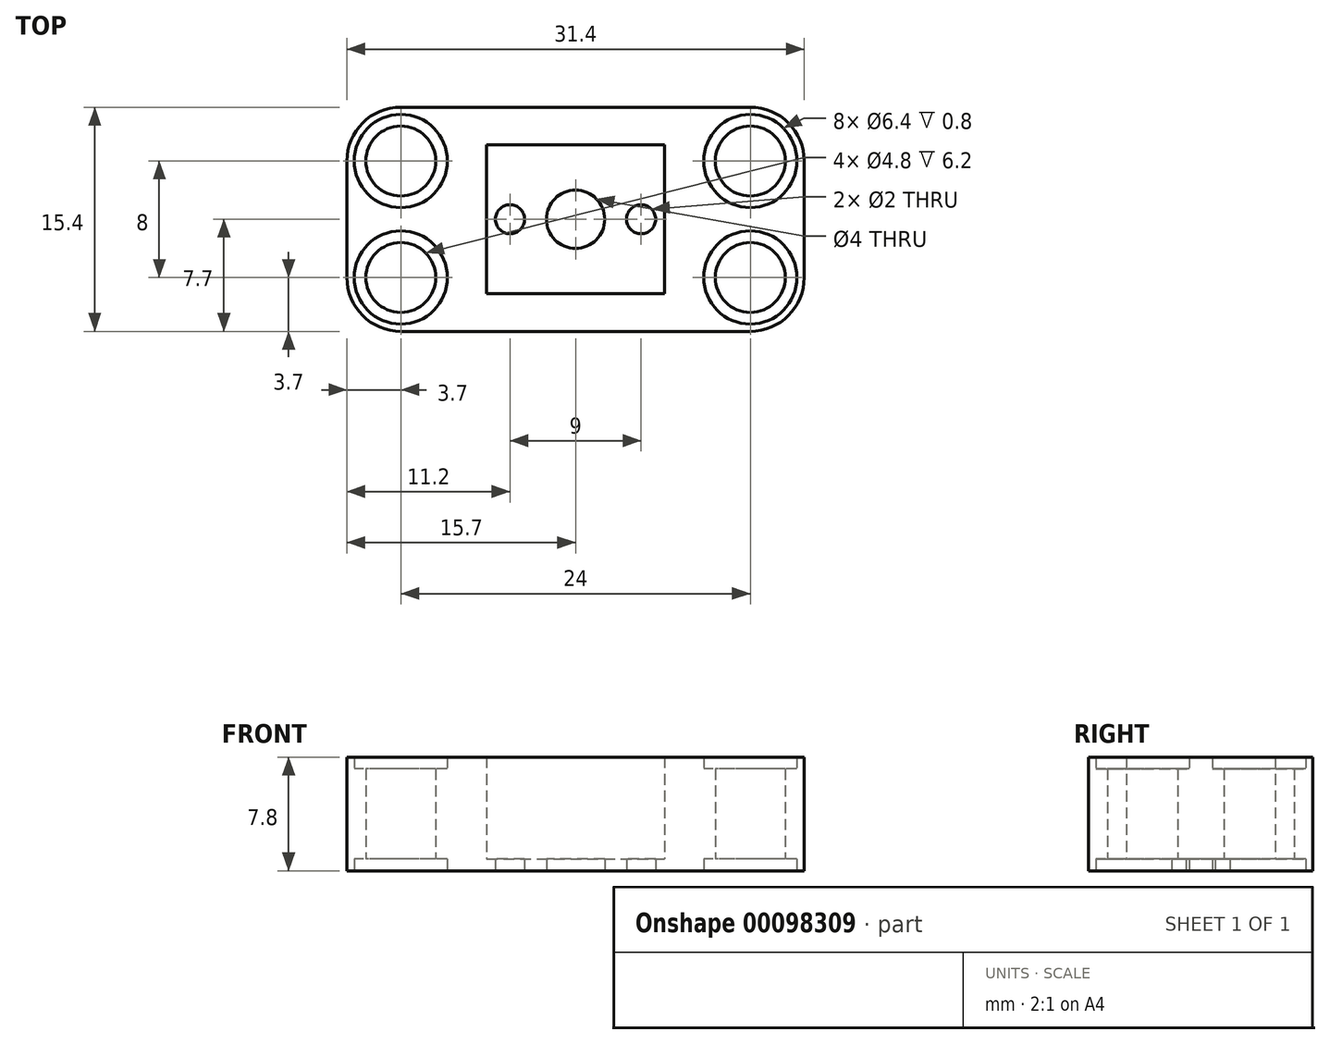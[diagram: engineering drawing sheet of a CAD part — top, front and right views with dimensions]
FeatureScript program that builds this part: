
annotation { "Feature Type Name" : "Feature", "Feature Type Description" : "" }
export const myFeature = defineFeature(function(context is Context, id is Id, definition is map)
    precondition{}
    {
        {
            var Q0;
            Q0=qCreatedBy(makeId("Top.planeOp"),FACE);
            var sketch = newSketch(context, id + "F0", { "sketchPlane" : qUnion([Q0])});
            skLineSegment(sketch, "E0.bottom", {"start": v(-12, 7.7) * mm, "end": v(12, 7.7) * mm});
            skLineSegment(sketch, "E0.top", {"start": v(-12, -7.7) * mm, "end": v(12, -7.7) * mm});
            skLineSegment(sketch, "E0.left", {"start": v(-15.7, 4) * mm, "end": v(-15.7, -4) * mm});
            skLineSegment(sketch, "E0.right", {"start": v(15.7, 4) * mm, "end": v(15.7, -4) * mm});
            skPoint(sketch, "E1.visualSharp", {"position": v(15.7, 7.7) * mm});
            skArc(sketch, "E1.filletArc", {"start": v(15.7, 4) * mm, "mid": v(14.62, 6.62) * mm, "end": v(12, 7.7) * mm});
            skPoint(sketch, "E2.visualSharp", {"position": v(15.7, -7.7) * mm});
            skArc(sketch, "E2.filletArc", {"start": v(12, -7.7) * mm, "mid": v(14.62, -6.62) * mm, "end": v(15.7, -4) * mm});
            skPoint(sketch, "E3.visualSharp", {"position": v(-15.7, -7.7) * mm});
            skArc(sketch, "E3.filletArc", {"start": v(-15.7, -4) * mm, "mid": v(-14.62, -6.62) * mm, "end": v(-12, -7.7) * mm});
            skPoint(sketch, "E4.visualSharp", {"position": v(-15.7, 7.7) * mm});
            skArc(sketch, "E4.filletArc", {"start": v(-12, 7.7) * mm, "mid": v(-14.62, 6.62) * mm, "end": v(-15.7, 4) * mm});
            skCircle(sketch, "E5", {"center": v(-12, 4) * mm, "radius": 3.2 * mm});
            skCircle(sketch, "E6", {"center": v(-12, 4) * mm, "radius": 2.4 * mm});
            skCircle(sketch, "E7", {"center": v(12, 4) * mm, "radius": 2.4 * mm});
            skCircle(sketch, "E8", {"center": v(12, 4) * mm, "radius": 3.2 * mm});
            skCircle(sketch, "E9", {"center": v(-12, -4) * mm, "radius": 2.4 * mm});
            skCircle(sketch, "E10", {"center": v(-12, -4) * mm, "radius": 3.2 * mm});
            skCircle(sketch, "E11", {"center": v(12, -4) * mm, "radius": 2.4 * mm});
            skCircle(sketch, "E12", {"center": v(12, -4) * mm, "radius": 3.2 * mm});
            skLineSegment(sketch, "E13.bottom", {"start": v(-6.1, 5.1) * mm, "end": v(6.1, 5.1) * mm});
            skLineSegment(sketch, "E13.top", {"start": v(-6.1, -5.1) * mm, "end": v(6.1, -5.1) * mm});
            skLineSegment(sketch, "E13.left", {"start": v(-6.1, 5.1) * mm, "end": v(-6.1, -5.1) * mm});
            skLineSegment(sketch, "E13.right", {"start": v(6.1, 5.1) * mm, "end": v(6.1, -5.1) * mm});
            skCircle(sketch, "E14", {"center": v(0, 0) * mm, "radius": 2 * mm});
            skCircle(sketch, "E15", {"center": v(4.5, 0) * mm, "radius": 1 * mm});
            skCircle(sketch, "E16", {"center": v(-4.5, 0) * mm, "radius": 1 * mm});
            skSolve(sketch);
        }
        {
            var Q0;
            Q0=makeQuery(id+"F0.imprint","IMPRINT",FACE,{"disambiguationData":[TD([[makeQuery(id+"F0.imprint","IMPRINT",EDGE,{"derivedFrom":sQuery(id+"F0.wireOp",EDGE,"E0.bottom")}),-1.0]])]});
            extrude(context, id + "F1", {"entities" : qUnion([Q0]), "depth" : 7.8 * mm});
        }
        {
            var Q0;
            Q0=makeQuery(id+"F0.imprint","IMPRINT",FACE,{"disambiguationData":[TD([[makeQuery(id+"F0.imprint","IMPRINT",EDGE,{"derivedFrom":sQuery(id+"F0.wireOp",EDGE,"E9")}),-1.0]])]});
            var Q1;
            Q1=makeQuery(id+"F0.imprint","IMPRINT",FACE,{"disambiguationData":[TD([[makeQuery(id+"F0.imprint","IMPRINT",EDGE,{"derivedFrom":sQuery(id+"F0.wireOp",EDGE,"E11")}),-1.0]])]});
            var Q2;
            Q2=makeQuery(id+"F0.imprint","IMPRINT",FACE,{"disambiguationData":[TD([[makeQuery(id+"F0.imprint","IMPRINT",EDGE,{"derivedFrom":sQuery(id+"F0.wireOp",EDGE,"E5")}),1.0]])]});
            var Q3;
            Q3=makeQuery(id+"F0.imprint","IMPRINT",FACE,{"disambiguationData":[TD([[makeQuery(id+"F0.imprint","IMPRINT",EDGE,{"derivedFrom":sQuery(id+"F0.wireOp",EDGE,"E7")}),-1.0]])]});
            extrude(context, id + "F2", {"entities" : qUnion([Q0, Q1, Q2, Q3]), "operationType" : NewBodyOperationType.ADD, "depth" : 7 * mm, "hasSecondDirection" : true, "secondDirectionOppositeDirection" : false, "secondDirectionDepth" : 0.8 * mm});
        }
        {
            var Q0;
            Q0=makeQuery(id+"F0.imprint","IMPRINT",FACE,{"disambiguationData":[TD([[makeQuery(id+"F0.imprint","IMPRINT",EDGE,{"derivedFrom":sQuery(id+"F0.wireOp",EDGE,"E13.bottom")}),-1.0]])]});
            extrude(context, id + "F3", {"entities" : qUnion([Q0]), "operationType" : NewBodyOperationType.ADD, "depth" : 0.8 * mm});
        }
    });
